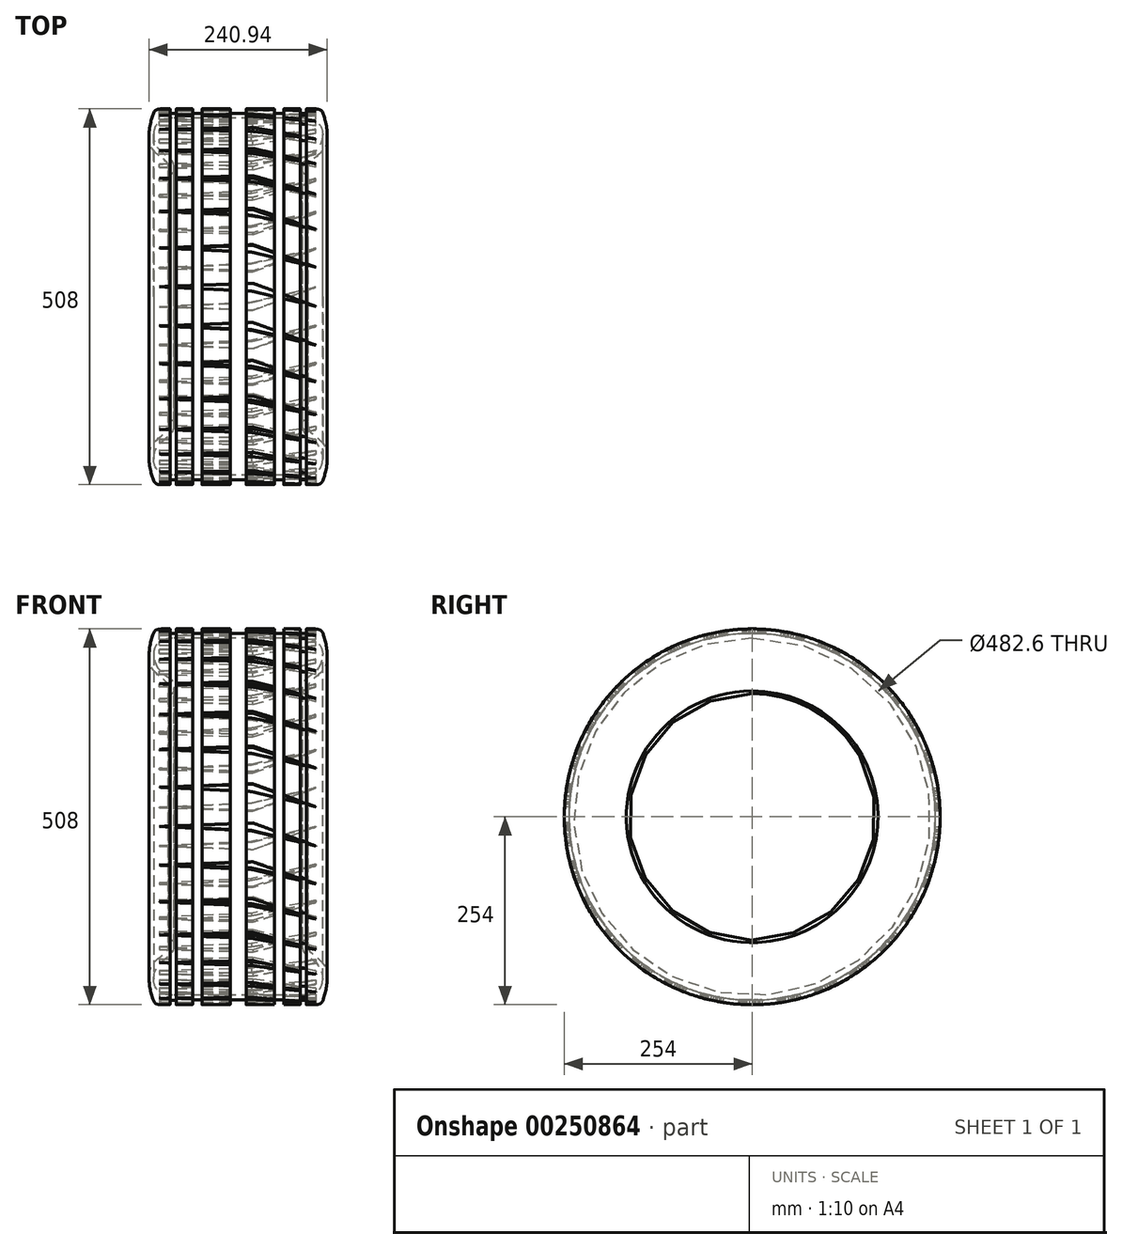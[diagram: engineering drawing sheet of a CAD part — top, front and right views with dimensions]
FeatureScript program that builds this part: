
annotation { "Feature Type Name" : "Feature", "Feature Type Description" : "" }
export const myFeature = defineFeature(function(context is Context, id is Id, definition is map)
    precondition{}
    {
        {
            var Q0;
            Q0=qCreatedBy(makeId("Front.planeOp"),FACE);
            var sketch = newSketch(context, id + "F0", { "sketchPlane" : qUnion([Q0])});
            skLineSegment(sketch, "E0", {"start": v(0, 0) * mm, "end": v(101.6, 0) * mm});
            skLineSegment(sketch, "E1", {"start": v(0, 12.7) * mm, "end": v(88.9, 12.7) * mm});
            skLineSegment(sketch, "E2", {"start": v(0, 12.7) * mm, "end": v(0, 0) * mm});
            skFitSpline(sketch, "E3", {"points": [v(88.9, 12.7) * mm, v(113.31, 27.68) * mm, v(106.52, 55.25) * mm, v(88.9, 70.88) * mm, v(86.77, 83.85) * mm], "startDerivative": vector(148.91, -0.67) * mm, "endDerivative": vector(0.67, 65.93) * mm});
            skFitSpline(sketch, "E4", {"points": [v(101.6, 0) * mm, v(114.96, 7.1) * mm, v(118.04, 49.9) * mm, v(96.23, 72.94) * mm, v(94.18, 83.85) * mm], "startDerivative": vector(147.56, 0) * mm, "endDerivative": vector(4.13, 64.2) * mm});
            skArc(sketch, "E5", {"start": v(94.18, 83.85) * mm, "mid": v(90.47, 87.4) * mm, "end": v(86.77, 83.85) * mm});
            skLineSegment(sketch, "E6", {"start": v(-94.18, 254) * mm, "end": v(94.18, 254) * mm});
            skLineSegment(sketch, "E7.MirrorCS", {"start": v(0, 0) * mm, "end": v(-101.6, 0) * mm});
            skLineSegment(sketch, "E8.MirrorCS", {"start": v(0, 12.7) * mm, "end": v(-88.9, 12.7) * mm});
            skFitSpline(sketch, "E9.MirrorCS", {"points": [v(-88.9, 12.7) * mm, v(-113.31, 27.68) * mm, v(-106.52, 55.25) * mm, v(-88.9, 70.88) * mm, v(-86.77, 83.85) * mm], "startDerivative": vector(-148.91, -0.67) * mm, "endDerivative": vector(-0.67, 65.93) * mm});
            skFitSpline(sketch, "E10.MirrorCS", {"points": [v(-101.6, 0) * mm, v(-114.96, 7.1) * mm, v(-118.04, 49.9) * mm, v(-96.23, 72.94) * mm, v(-94.18, 83.85) * mm], "startDerivative": vector(-147.56, 0) * mm, "endDerivative": vector(-4.13, 64.2) * mm});
            skArc(sketch, "E11.MirrorCS", {"start": v(-94.18, 83.85) * mm, "mid": v(-90.47, 87.4) * mm, "end": v(-86.77, 83.85) * mm});
            skSolve(sketch);
        }
        {
            var Q0;
            Q0 = qSketchRegion(id + "F0", true);
            var Q1;
            Q1=sQuery(id+"F0.wireOp",EDGE,"E6");
            revolve(context, id + "F1", {"entities" : qUnion([Q0]), "axis" : qUnion([Q1]), "revolveType" : RevolveType.FULL});
        }
        {
            var Q0;
            Q0=qCreatedBy(makeId("Front.planeOp"),FACE);
            var sketch = newSketch(context, id + "F2", { "sketchPlane" : qUnion([Q0])});
            skLineSegment(sketch, "E12", {"start": v(-10.8, 6.35) * mm, "end": v(-10.8, 0) * mm});
            skLineSegment(sketch, "E13", {"start": v(-48.9, 6.35) * mm, "end": v(-48.9, 0) * mm});
            skLineSegment(sketch, "E14", {"start": v(-61.6, 6.35) * mm, "end": v(-61.6, 0) * mm});
            skLineSegment(sketch, "E15", {"start": v(-92.08, 6.24) * mm, "end": v(-92.08, 0) * mm});
            skLineSegment(sketch, "E16", {"start": v(-83.82, 6.24) * mm, "end": v(-83.82, 0) * mm});
            skLineSegment(sketch, "E17.MirrorCS", {"start": v(10.8, 6.35) * mm, "end": v(10.8, 0) * mm});
            skLineSegment(sketch, "E18.MirrorCS", {"start": v(48.9, 6.35) * mm, "end": v(48.9, 0) * mm});
            skLineSegment(sketch, "E19.MirrorCS", {"start": v(61.6, 6.35) * mm, "end": v(61.6, 0) * mm});
            skLineSegment(sketch, "E20.MirrorCS", {"start": v(83.82, 6.24) * mm, "end": v(83.82, 0) * mm});
            skLineSegment(sketch, "E21.MirrorCS", {"start": v(92.08, 6.24) * mm, "end": v(92.08, 0) * mm});
            skLineSegment(sketch, "E22", {"start": v(83.82, 6.24) * mm, "end": v(92.08, 6.24) * mm});
            skLineSegment(sketch, "E23", {"start": v(-92.08, 6.24) * mm, "end": v(-83.82, 6.24) * mm});
            skLineSegment(sketch, "E24", {"start": v(-162.71, 254) * mm, "end": v(142.5, 254) * mm});
            skLineSegment(sketch, "E25", {"start": v(-92.08, 0) * mm, "end": v(-83.82, 0) * mm});
            skLineSegment(sketch, "E26", {"start": v(-61.6, 0) * mm, "end": v(-48.9, 0) * mm});
            skLineSegment(sketch, "E27", {"start": v(-10.8, 0) * mm, "end": v(10.8, 0) * mm});
            skLineSegment(sketch, "E28", {"start": v(48.9, 0) * mm, "end": v(61.6, 0) * mm});
            skLineSegment(sketch, "E29", {"start": v(83.82, 0) * mm, "end": v(92.08, 0) * mm});
            skLineSegment(sketch, "E30", {"start": v(-61.6, 6.35) * mm, "end": v(-48.9, 6.35) * mm});
            skLineSegment(sketch, "E31", {"start": v(-10.8, 6.35) * mm, "end": v(10.8, 6.35) * mm});
            skLineSegment(sketch, "E32", {"start": v(48.9, 6.35) * mm, "end": v(61.6, 6.35) * mm});
            skSolve(sketch);
        }
        {
            var Q0;
            Q0 = qSketchRegion(id + "F2", true);
            var Q1;
            Q1=sQuery(id+"F2.wireOp",EDGE,"E24");
            revolve(context, id + "F3", {"operationType" : NewBodyOperationType.REMOVE, "entities" : qUnion([Q0]), "axis" : qUnion([Q1]), "revolveType" : RevolveType.FULL, "oppositeDirection" : true});
        }
        {
            var Q0;
            Q0=sQuery(id+"F2.wireOp",EDGE,"E24");
            var Q1;
            Q1=sQuery(id+"F2.wireOp",VERTEX,"E12.end");
            cPlane(context, id + "F4", {"entities" : qUnion([Q0, Q1]), "cplaneType" : CPlaneType.LINE_ANGLE, "offset" : 25.4 * mm, "angle" : 90 * degree, "width" : 152.4 * mm, "height" : 152.4 * mm});
        }
        {
            var Q0;
            Q0=qCreatedBy(id+"F4.planeOp",FACE);
            cPlane(context, id + "F5", {"entities" : qUnion([Q0]), "cplaneType" : CPlaneType.OFFSET, "offset" : 254 * mm, "width" : 152.4 * mm, "height" : 152.4 * mm});
        }
        {
            var Q0;
            Q0=qCreatedBy(id+"F5.planeOp",FACE);
            var sketch = newSketch(context, id + "F6", { "sketchPlane" : qUnion([Q0])});
            skLineSegment(sketch, "E33", {"start": v(-106.36, 13.56) * mm, "end": v(20.09, 18.26) * mm});
            skLineSegment(sketch, "E34", {"start": v(20.09, 18.26) * mm, "end": v(105.22, -13.04) * mm});
            skLineSegment(sketch, "E35", {"start": v(105.22, -13.04) * mm, "end": v(18.2, 7.62) * mm});
            skLineSegment(sketch, "E36", {"start": v(18.2, 7.62) * mm, "end": v(-106.36, 13.56) * mm});
            skSolve(sketch);
        }
        {
            var Q0;
            Q0=makeQuery(id+"F6.imprint","IMPRINT",FACE,{"disambiguationData":[TD([[makeQuery(id+"F6.imprint","IMPRINT",EDGE,{"derivedFrom":sQuery(id+"F6.wireOp",EDGE,"E33")}),-1.0]])]});
            extrude(context, id + "F7", {"entities" : qUnion([Q0]), "oppositeDirection" : true, "depth" : 6.35 * mm});
        }
        {
            var Q0;
            Q0=makeQuery(id+"F7.opExtrude","SWEPT_BODY",BODY,{"disambiguationData":[OSD([sQuery(id+"F6.wireOp",EDGE,"E33"),sQuery(id+"F6.wireOp",EDGE,"E34"),sQuery(id+"F6.wireOp",EDGE,"E35"),sQuery(id+"F6.wireOp",EDGE,"E36")])]});
            var Q1;
            Q1=sQuery(id+"F2.wireOp",EDGE,"E24");
            circularPattern(context, id + "F8", {"operationType" : NewBodyOperationType.REMOVE, "entities" : qUnion([Q0]), "axis" : qUnion([Q1]), "angle" : 360 * degree, "instanceCount" : 30, "equalSpace" : true});
        }
    });
